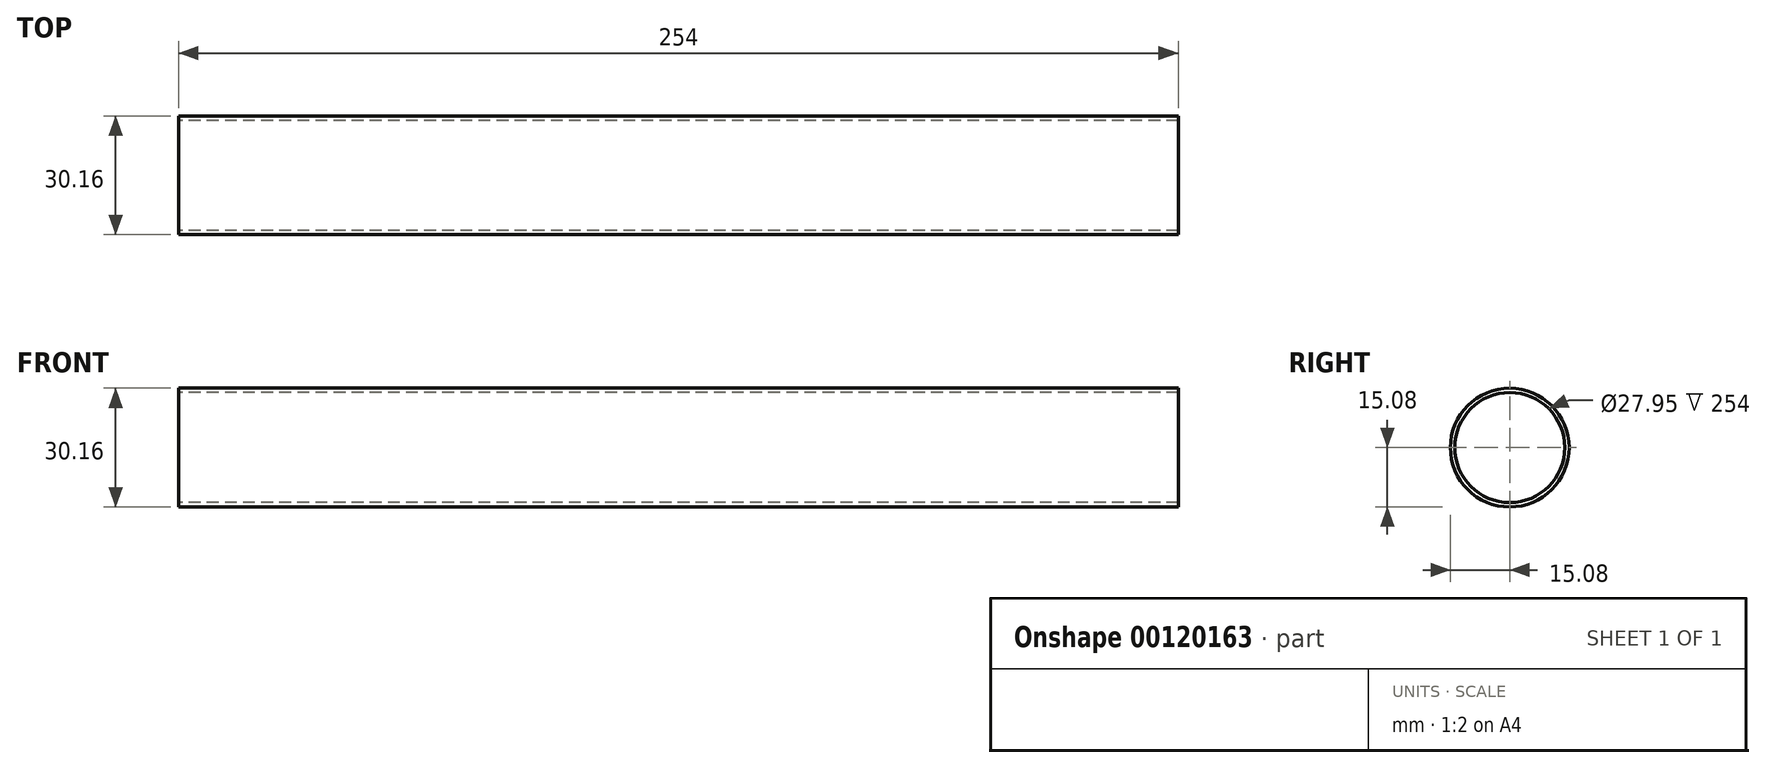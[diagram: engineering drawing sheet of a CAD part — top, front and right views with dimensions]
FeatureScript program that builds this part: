
annotation { "Feature Type Name" : "Feature", "Feature Type Description" : "" }
export const myFeature = defineFeature(function(context is Context, id is Id, definition is map)
    precondition{}
    {
        {
            var Q0;
            Q0=qCreatedBy(makeId("Right.planeOp"),FACE);
            var sketch = newSketch(context, id + "F0", { "sketchPlane" : qUnion([Q0])});
            skCircle(sketch, "E0", {"center": v(0, 0) * mm, "radius": 15.08 * mm});
            skCircle(sketch, "E1", {"center": v(0, 0) * mm, "radius": 13.97 * mm});
            skSolve(sketch);
        }
        {
            var Q0;
            Q0=makeQuery(id+"F0.imprint","IMPRINT",FACE,{"disambiguationData":[TD([[makeQuery(id+"F0.imprint","IMPRINT",EDGE,{"derivedFrom":sQuery(id+"F0.wireOp",EDGE,"E0")}),1.0]])]});
            extrude(context, id + "F1", {"entities" : qUnion([Q0]), "depth" : 254 * mm});
        }
        {
            var Q0;
            Q0=qCreatedBy(makeId("Front.planeOp"),FACE);
            var sketch = newSketch(context, id + "F2", { "sketchPlane" : qUnion([Q0])});
            skLineSegment(sketch, "E2", {"start": v(0, 0) * mm, "end": v(-86.9, 0) * mm});
            skFitSpline(sketch, "E3", {"points": [v(-86.9, 0) * mm, v(-128.32, 0) * mm, v(-168.93, -11.67) * mm, v(-194.5, -36.84) * mm, v(-210.75, -88.41) * mm, v(-198.98, -110.75) * mm, v(-158.37, -135.92) * mm, v(-86.9, -134.7) * mm], "startDerivative": vector(-296.6, 17.16) * mm, "endDerivative": vector(419.07, 58.56) * mm});
            skSolve(sketch);
        }
    });
